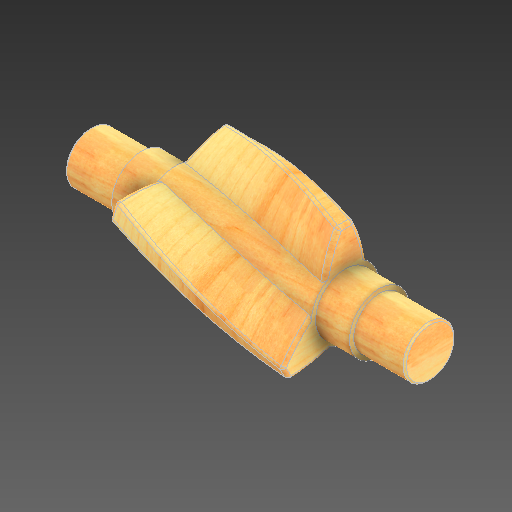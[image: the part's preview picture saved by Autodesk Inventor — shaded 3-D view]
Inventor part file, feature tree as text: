
AUTODESK INVENTOR PART (.ipt)
format: ipt  version: 2020 (Build 240168000, 168)  size: 702,464 bytes
history: native  units: mm
features: other x4, extrude x1, chamfer x1, sketch x1
ambient origin geometry x8: Origin, YZ Plane, XZ Plane, XY Plane, X Axis, Y Axis, Z Axis, Center Point
bodies: Body1 (feature_tree)
feature tree (7):
  other  "WormA.ipt"
  extrude  "擠出1"  Depth=110.0mm
  chamfer  "倒角1"  Distance=33.0mm
  other  "實體1::WormA.ipt"
  other  "標籤特徵1"
  sketch  "草圖1"
  other  "實體1"
